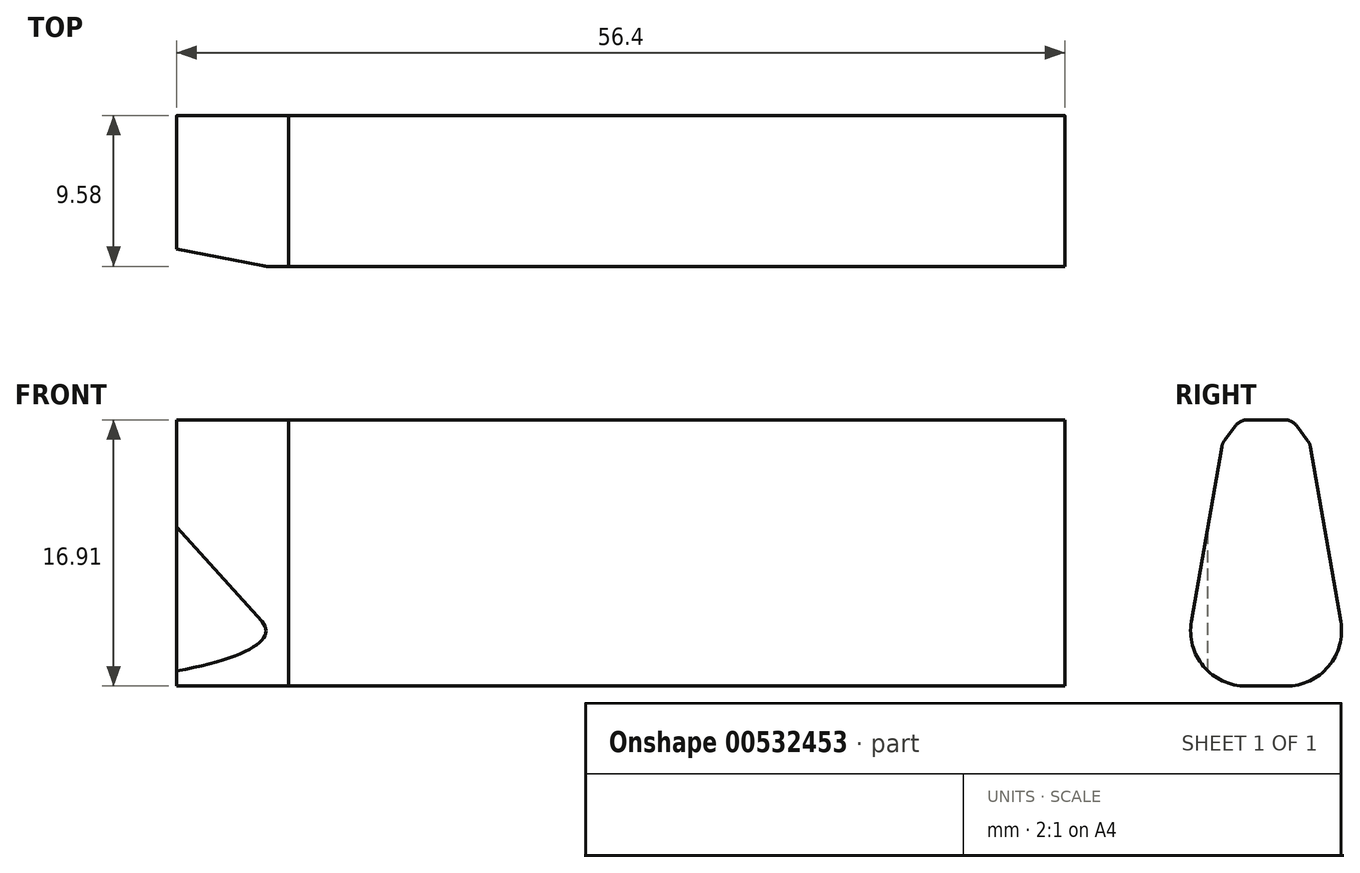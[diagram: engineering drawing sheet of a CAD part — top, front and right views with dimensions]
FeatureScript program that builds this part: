
annotation { "Feature Type Name" : "Feature", "Feature Type Description" : "" }
export const myFeature = defineFeature(function(context is Context, id is Id, definition is map)
    precondition{}
    {
        {
            var Q0;
            Q0=qCreatedBy(makeId("Front.planeOp"),FACE);
            var sketch = newSketch(context, id + "F0", { "sketchPlane" : qUnion([Q0])});
            skLineSegment(sketch, "E0", {"start": v(-77.65, 28.33) * mm, "end": v(-77.65, 11.36) * mm});
            skLineSegment(sketch, "E1", {"start": v(-28.03, 28.5) * mm, "end": v(-28.03, 11.04) * mm});
            skSolve(sketch);
        }
        {
            var Q0;
            Q0=sQuery(id+"F0.wireOp",EDGE,"E0");
            cPlane(context, id + "F1", {"entities" : qUnion([Q0]), "cplaneType" : CPlaneType.LINE_ANGLE, "offset" : 25 * mm, "angle" : 0 * degree, "width" : 150 * mm, "height" : 150 * mm});
        }
        {
            var Q0;
            Q0=qCreatedBy(id+"F1.planeOp",FACE);
            var sketch = newSketch(context, id + "F2", { "sketchPlane" : qUnion([Q0])});
            skPoint(sketch, "E2.0", {"position": v(0, 28.33) * mm});
            skPoint(sketch, "E3.0", {"position": v(0, 11.36) * mm});
            skLineSegment(sketch, "E4", {"start": v(0, 28.33) * mm, "end": v(1.16, 28.33) * mm});
            skLineSegment(sketch, "E5", {"start": v(1.96, 27.93) * mm, "end": v(2.64, 27.02) * mm});
            skLineSegment(sketch, "E6", {"start": v(2.82, 26.6) * mm, "end": v(4.74, 15.52) * mm});
            skLineSegment(sketch, "E7", {"start": v(1.3, 11.42) * mm, "end": v(0, 11.42) * mm});
            skPoint(sketch, "E8.visualSharp", {"position": v(5.45, 11.42) * mm});
            skArc(sketch, "E8.filletArc", {"start": v(1.3, 11.42) * mm, "mid": v(3.97, 12.67) * mm, "end": v(4.74, 15.52) * mm});
            skPoint(sketch, "E9.visualSharp", {"position": v(1.66, 28.33) * mm});
            skArc(sketch, "E9.filletArc", {"start": v(1.96, 27.93) * mm, "mid": v(1.6, 28.23) * mm, "end": v(1.16, 28.33) * mm});
            skPoint(sketch, "E10.visualSharp", {"position": v(2.78, 26.83) * mm});
            skArc(sketch, "E10.filletArc", {"start": v(2.82, 26.6) * mm, "mid": v(2.75, 26.82) * mm, "end": v(2.64, 27.02) * mm});
            skLineSegment(sketch, "E11", {"start": v(0, 28.33) * mm, "end": v(0, 11.42) * mm});
            skSolve(sketch);
        }
        {
            var Q0;
            Q0=makeQuery(id+"F2.imprint","IMPRINT",FACE,{"disambiguationData":[TD([[makeQuery(id+"F2.imprint","IMPRINT",EDGE,{"derivedFrom":sQuery(id+"F2.wireOp",EDGE,"E4")}),-1.0]])]});
            extrude(context, id + "F3", {"entities" : qUnion([Q0]), "oppositeDirection" : true, "depth" : 49.3 * mm, "offsetDistance" : 25 * mm});
        }
        {
            var Q0;
            Q0=makeQuery(id+"F3.opExtrude","SWEPT_BODY",BODY,{"disambiguationData":[OSD([sQuery(id+"F2.wireOp",EDGE,"E4"),sQuery(id+"F2.wireOp",EDGE,"E5"),sQuery(id+"F2.wireOp",EDGE,"E6"),sQuery(id+"F2.wireOp",EDGE,"E7"),sQuery(id+"F2.wireOp",EDGE,"E8.filletArc"),sQuery(id+"F2.wireOp",EDGE,"E9.filletArc"),sQuery(id+"F2.wireOp",EDGE,"E10.filletArc"),sQuery(id+"F2.wireOp",EDGE,"E11")])]});
            var Q1;
            Q1=makeQuery(id+"F3.opExtrude","SWEPT_FACE",FACE,{"disambiguationData":[OSD([sQuery(id+"F2.wireOp",EDGE,"E11")])]});
            mirror(context, id + "F4", {"operationType" : NewBodyOperationType.ADD, "entities" : qUnion([Q0]), "mirrorPlane" : qUnion([Q1])});
        }
        {
            var Q0;
            {var subQ0=makeQuery(id+"F3.opExtrude","CAP_FACE",FACE,{"disambiguationData":[OSD([sQuery(id+"F2.wireOp",EDGE,"E4"),sQuery(id+"F2.wireOp",EDGE,"E5"),sQuery(id+"F2.wireOp",EDGE,"E6"),sQuery(id+"F2.wireOp",EDGE,"E7"),sQuery(id+"F2.wireOp",EDGE,"E8.filletArc"),sQuery(id+"F2.wireOp",EDGE,"E9.filletArc"),sQuery(id+"F2.wireOp",EDGE,"E10.filletArc"),sQuery(id+"F2.wireOp",EDGE,"E11")])],"isStart":true});Q0=makeQuery(id+"F4.boolean.opBoolean","MERGE",FACE,{"derivedFrom":[subQ0,makeQuery(id+"F4.opPattern","COPY",FACE,{"derivedFrom":subQ0,"instanceName":"1"})]});}
            extrude(context, id + "F5", {"entities" : qUnion([Q0]), "depth" : 7.1 * mm, "offsetDistance" : 25 * mm});
        }
        {
            var Q0;
            Q0=qCreatedBy(makeId("Top.planeOp"),FACE);
            cPlane(context, id + "F6", {"entities" : qUnion([Q0]), "cplaneType" : CPlaneType.OFFSET, "offset" : 39.6 * mm, "width" : 150 * mm, "height" : 150 * mm});
        }
        {
            var Q0;
            Q0=qCreatedBy(id+"F6.planeOp",FACE);
            var sketch = newSketch(context, id + "F7", { "sketchPlane" : qUnion([Q0])});
            skLineSegment(sketch, "E12", {"start": v(-85.3, -3.6) * mm, "end": v(-77.95, -5) * mm});
            skLineSegment(sketch, "E13", {"start": v(-77.95, -5) * mm, "end": v(-78.5, -8.4) * mm});
            skLineSegment(sketch, "E14", {"start": v(-78.5, -8.4) * mm, "end": v(-83.67, -8.15) * mm});
            skLineSegment(sketch, "E15", {"start": v(-83.67, -8.15) * mm, "end": v(-88.28, -6.05) * mm});
            skLineSegment(sketch, "E16", {"start": v(-88.28, -6.05) * mm, "end": v(-85.3, -3.6) * mm});
            skSolve(sketch);
        }
        {
            var Q0;
            Q0=makeQuery(id+"F7.imprint","IMPRINT",FACE,{"disambiguationData":[TD([[makeQuery(id+"F7.imprint","IMPRINT",EDGE,{"derivedFrom":sQuery(id+"F7.wireOp",EDGE,"E12")}),-1.0]])]});
            extrude(context, id + "F8", {"entities" : qUnion([Q0]), "operationType" : NewBodyOperationType.REMOVE, "oppositeDirection" : true, "depth" : 32.13 * mm, "offsetDistance" : 25 * mm});
        }
    });
